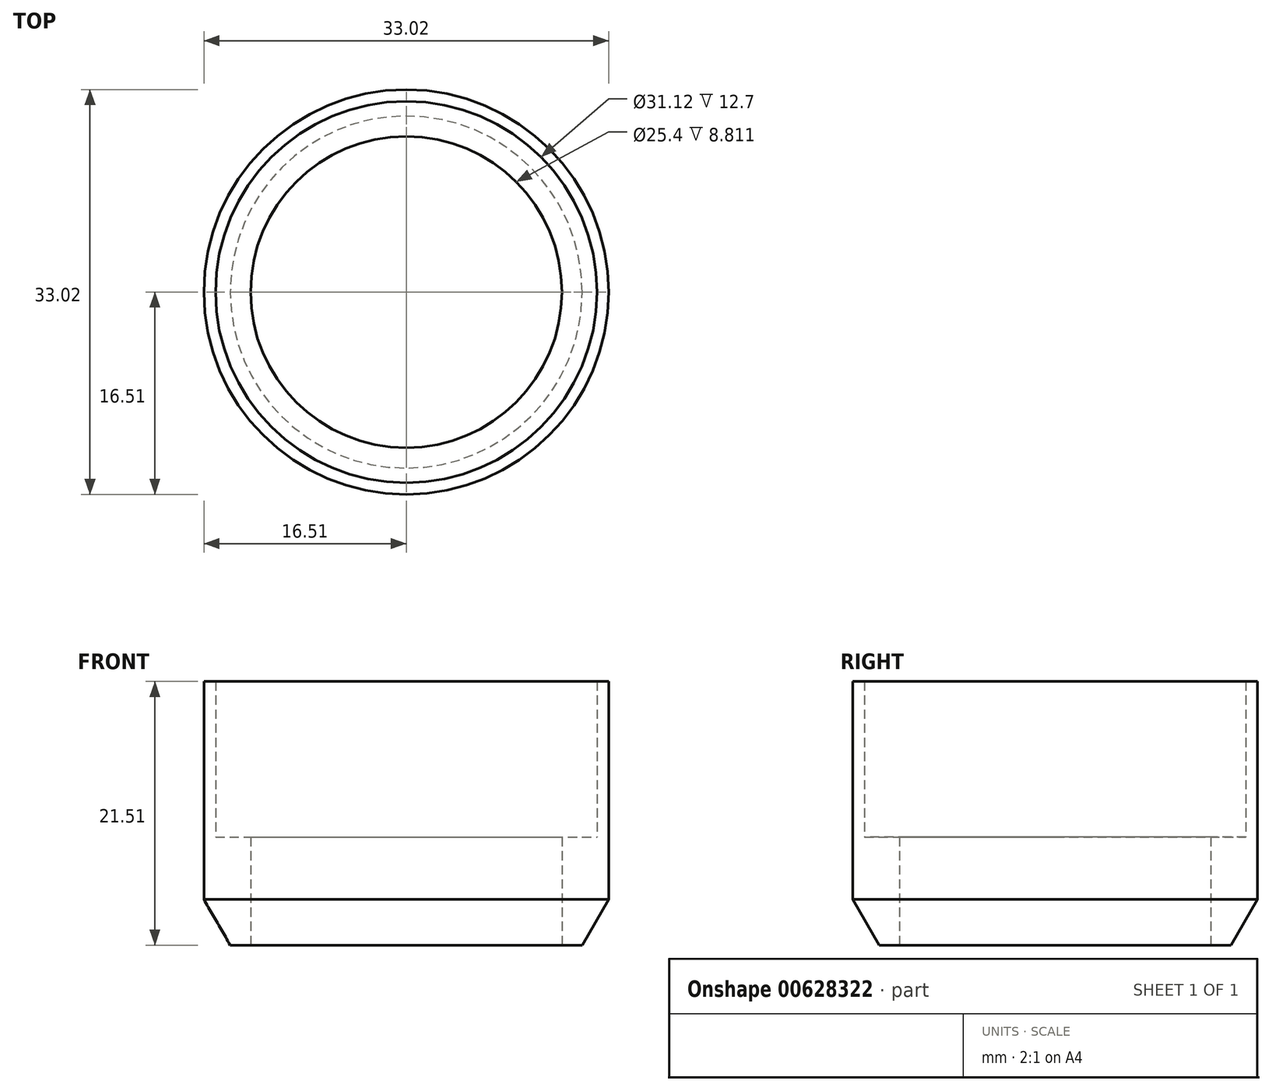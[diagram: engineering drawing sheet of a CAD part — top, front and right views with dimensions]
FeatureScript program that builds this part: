
annotation { "Feature Type Name" : "Feature", "Feature Type Description" : "" }
export const myFeature = defineFeature(function(context is Context, id is Id, definition is map)
    precondition{}
    {
        {
            var Q0;
            Q0=qCreatedBy(makeId("Front.planeOp"),FACE);
            var sketch = newSketch(context, id + "F0", { "sketchPlane" : qUnion([Q0])});
            skLineSegment(sketch, "E0", {"start": v(16.51, -5.08) * mm, "end": v(14.36, -8.81) * mm});
            skLineSegment(sketch, "E1", {"start": v(14.36, -8.81) * mm, "end": v(12.7, -8.81) * mm});
            skLineSegment(sketch, "E2", {"start": v(12.7, -8.81) * mm, "end": v(12.7, 0) * mm});
            skLineSegment(sketch, "E3", {"start": v(12.7, 0) * mm, "end": v(15.56, 0) * mm});
            skLineSegment(sketch, "E4", {"start": v(15.56, 0) * mm, "end": v(15.56, 12.7) * mm});
            skLineSegment(sketch, "E5", {"start": v(15.56, 12.7) * mm, "end": v(16.5, 12.7) * mm});
            skLineSegment(sketch, "E6", {"start": v(16.51, 12.7) * mm, "end": v(16.51, -5.08) * mm});
            skLineSegment(sketch, "E7", {"start": v(0, 0) * mm, "end": v(0, 17.41) * mm});
            skSolve(sketch);
        }
        {
            var Q0;
            Q0=makeQuery(id+"F0.imprint","IMPRINT",FACE,{"disambiguationData":[TD([[makeQuery(id+"F0.imprint","IMPRINT",EDGE,{"derivedFrom":sQuery(id+"F0.wireOp",EDGE,"E0")}),-1.0]])]});
            var Q1;
            Q1=sQuery(id+"F0.wireOp",EDGE,"E7");
            revolve(context, id + "F1", {"entities" : qUnion([Q0]), "axis" : qUnion([Q1]), "revolveType" : RevolveType.FULL});
        }
    });
